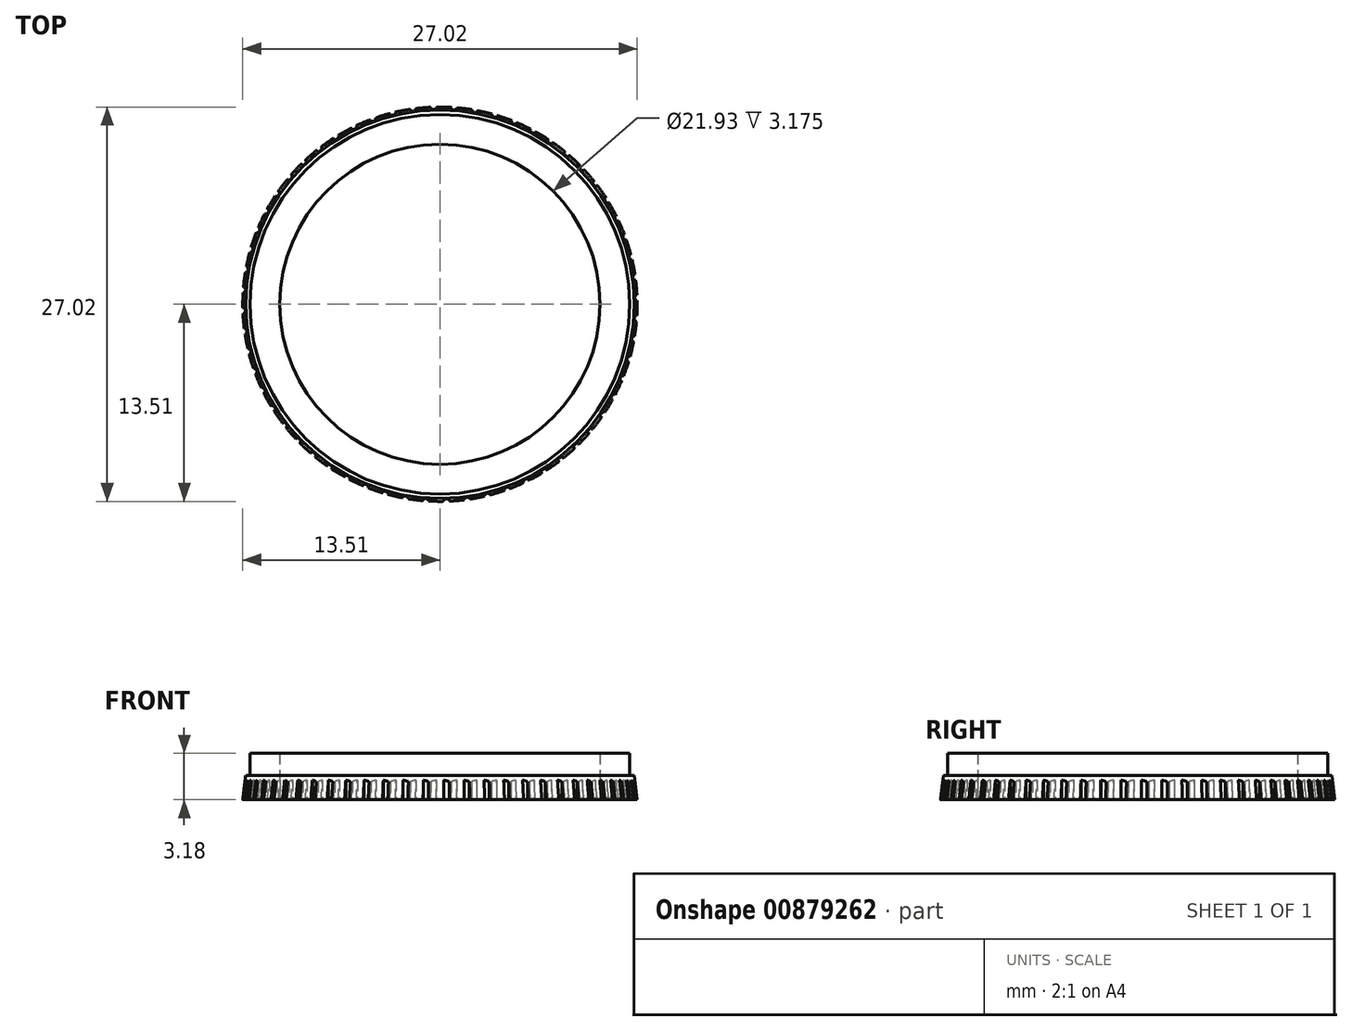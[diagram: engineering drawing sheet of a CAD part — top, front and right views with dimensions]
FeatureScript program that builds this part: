
annotation { "Feature Type Name" : "Feature", "Feature Type Description" : "" }
export const myFeature = defineFeature(function(context is Context, id is Id, definition is map)
    precondition{}
    {
        {
            var Q0;
            Q0=qCreatedBy(makeId("Front.planeOp"),FACE);
            var sketch = newSketch(context, id + "F0", { "sketchPlane" : qUnion([Q0])});
            skLineSegment(sketch, "E0", {"start": v(0, -0.58) * mm, "end": v(0, 5.66) * mm, "construction": true});
            skLineSegment(sketch, "E1", {"start": v(10.97, 0) * mm, "end": v(10.97, 3.18) * mm});
            skLineSegment(sketch, "E2", {"start": v(10.97, 3.18) * mm, "end": v(13, 3.18) * mm});
            skLineSegment(sketch, "E3", {"start": v(13, 3.18) * mm, "end": v(13, 1.66) * mm});
            skLineSegment(sketch, "E4", {"start": v(13, 1.66) * mm, "end": v(13.3, 1.66) * mm});
            skLineSegment(sketch, "E5", {"start": v(13.3, 1.66) * mm, "end": v(13.5, 0) * mm});
            skLineSegment(sketch, "E6", {"start": v(13.5, 0) * mm, "end": v(10.97, 0) * mm});
            skSolve(sketch);
        }
        {
            var Q0;
            Q0=qSketchRegion(id+"F0",true);
            var Q1;
            Q1=sQuery(id+"F0.wireOp",EDGE,"E0");
            revolve(context, id + "F1", {"surfaceOperationType" : NewSurfaceOperationType.NEW, "entities" : qUnion([Q0]), "axis" : qUnion([Q1]), "revolveType" : RevolveType.FULL});
        }
        {
            var Q0;
            Q0=makeQuery(id+"F1.opRevolve","SWEPT_FACE",FACE,{"disambiguationData":[OSD([sQuery(id+"F0.wireOp",EDGE,"E6")])]});
            var sketch = newSketch(context, id + "F2", { "sketchPlane" : qUnion([Q0])});
            skLineSegment(sketch, "E7.bottom", {"start": v(0.26, 13.55) * mm, "end": v(0.63, 13.55) * mm});
            skLineSegment(sketch, "E7.top", {"start": v(0.26, 13.34) * mm, "end": v(0.63, 13.34) * mm});
            skLineSegment(sketch, "E7.left", {"start": v(0.26, 13.55) * mm, "end": v(0.26, 13.34) * mm});
            skLineSegment(sketch, "E7.right", {"start": v(0.63, 13.55) * mm, "end": v(0.63, 13.34) * mm});
            skLineSegment(sketch, "E8.1.0", {"start": v(-1.16, 13.5) * mm, "end": v(-1.14, 13.3) * mm});
            skLineSegment(sketch, "E8.1.1", {"start": v(-0.8, 13.54) * mm, "end": v(-0.77, 13.33) * mm});
            skLineSegment(sketch, "E8.1.2", {"start": v(-1.14, 13.3) * mm, "end": v(-0.77, 13.33) * mm});
            skLineSegment(sketch, "E8.1.3", {"start": v(-1.16, 13.5) * mm, "end": v(-0.8, 13.54) * mm});
            skLineSegment(sketch, "E8.2.0", {"start": v(-2.57, 13.3) * mm, "end": v(-2.52, 13.1) * mm});
            skLineSegment(sketch, "E8.2.1", {"start": v(-2.2, 13.38) * mm, "end": v(-2.16, 13.18) * mm});
            skLineSegment(sketch, "E8.2.2", {"start": v(-2.52, 13.1) * mm, "end": v(-2.16, 13.18) * mm});
            skLineSegment(sketch, "E8.2.3", {"start": v(-2.57, 13.3) * mm, "end": v(-2.2, 13.38) * mm});
            skLineSegment(sketch, "E8.3.0", {"start": v(-3.94, 12.96) * mm, "end": v(-3.88, 12.77) * mm});
            skLineSegment(sketch, "E8.3.1", {"start": v(-3.6, 13.08) * mm, "end": v(-3.53, 12.88) * mm});
            skLineSegment(sketch, "E8.3.2", {"start": v(-3.88, 12.77) * mm, "end": v(-3.53, 12.88) * mm});
            skLineSegment(sketch, "E8.3.3", {"start": v(-3.94, 12.96) * mm, "end": v(-3.6, 13.08) * mm});
            skLineSegment(sketch, "E8.4.0", {"start": v(-5.28, 12.48) * mm, "end": v(-5.2, 12.3) * mm});
            skLineSegment(sketch, "E8.4.1", {"start": v(-4.94, 12.63) * mm, "end": v(-4.85, 12.44) * mm});
            skLineSegment(sketch, "E8.4.2", {"start": v(-5.2, 12.3) * mm, "end": v(-4.85, 12.44) * mm});
            skLineSegment(sketch, "E8.4.3", {"start": v(-5.28, 12.48) * mm, "end": v(-4.94, 12.63) * mm});
            skLineSegment(sketch, "E8.5.0", {"start": v(-6.55, 11.86) * mm, "end": v(-6.45, 11.68) * mm});
            skLineSegment(sketch, "E8.5.1", {"start": v(-6.23, 12.04) * mm, "end": v(-6.13, 11.87) * mm});
            skLineSegment(sketch, "E8.5.2", {"start": v(-6.45, 11.68) * mm, "end": v(-6.13, 11.87) * mm});
            skLineSegment(sketch, "E8.5.3", {"start": v(-6.55, 11.86) * mm, "end": v(-6.23, 12.04) * mm});
            skLineSegment(sketch, "E8.6.0", {"start": v(-7.76, 11.1) * mm, "end": v(-7.64, 10.94) * mm});
            skLineSegment(sketch, "E8.6.1", {"start": v(-7.46, 11.33) * mm, "end": v(-7.34, 11.16) * mm});
            skLineSegment(sketch, "E8.6.2", {"start": v(-7.64, 10.94) * mm, "end": v(-7.34, 11.16) * mm});
            skLineSegment(sketch, "E8.6.3", {"start": v(-7.76, 11.1) * mm, "end": v(-7.46, 11.33) * mm});
            skLineSegment(sketch, "E8.7.0", {"start": v(-8.87, 10.24) * mm, "end": v(-8.74, 10.09) * mm});
            skLineSegment(sketch, "E8.7.1", {"start": v(-8.6, 10.49) * mm, "end": v(-8.46, 10.33) * mm});
            skLineSegment(sketch, "E8.7.2", {"start": v(-8.74, 10.09) * mm, "end": v(-8.46, 10.33) * mm});
            skLineSegment(sketch, "E8.7.3", {"start": v(-8.87, 10.24) * mm, "end": v(-8.6, 10.49) * mm});
            skLineSegment(sketch, "E8.8.0", {"start": v(-9.9, 9.25) * mm, "end": v(-9.74, 9.12) * mm});
            skLineSegment(sketch, "E8.8.1", {"start": v(-9.65, 9.53) * mm, "end": v(-9.5, 9.4) * mm});
            skLineSegment(sketch, "E8.8.2", {"start": v(-9.74, 9.12) * mm, "end": v(-9.5, 9.4) * mm});
            skLineSegment(sketch, "E8.8.3", {"start": v(-9.9, 9.25) * mm, "end": v(-9.65, 9.53) * mm});
            skLineSegment(sketch, "E8.9.0", {"start": v(-10.8, 8.17) * mm, "end": v(-10.64, 8.05) * mm});
            skLineSegment(sketch, "E8.9.1", {"start": v(-10.6, 8.47) * mm, "end": v(-10.43, 8.35) * mm});
            skLineSegment(sketch, "E8.9.2", {"start": v(-10.64, 8.05) * mm, "end": v(-10.43, 8.35) * mm});
            skLineSegment(sketch, "E8.9.3", {"start": v(-10.8, 8.17) * mm, "end": v(-10.6, 8.47) * mm});
            skLineSegment(sketch, "E8.10.0", {"start": v(-11.6, 7) * mm, "end": v(-11.43, 6.9) * mm});
            skLineSegment(sketch, "E8.10.1", {"start": v(-11.42, 7.32) * mm, "end": v(-11.24, 7.21) * mm});
            skLineSegment(sketch, "E8.10.2", {"start": v(-11.43, 6.9) * mm, "end": v(-11.24, 7.21) * mm});
            skLineSegment(sketch, "E8.10.3", {"start": v(-11.6, 7) * mm, "end": v(-11.42, 7.32) * mm});
            skLineSegment(sketch, "E8.11.0", {"start": v(-12.27, 5.74) * mm, "end": v(-12.08, 5.66) * mm});
            skLineSegment(sketch, "E8.11.1", {"start": v(-12.12, 6.08) * mm, "end": v(-11.93, 6) * mm});
            skLineSegment(sketch, "E8.11.2", {"start": v(-12.08, 5.66) * mm, "end": v(-11.93, 6) * mm});
            skLineSegment(sketch, "E8.11.3", {"start": v(-12.27, 5.74) * mm, "end": v(-12.12, 6.08) * mm});
            skLineSegment(sketch, "E8.12.0", {"start": v(-12.8, 4.43) * mm, "end": v(-12.6, 4.37) * mm});
            skLineSegment(sketch, "E8.12.1", {"start": v(-12.69, 4.78) * mm, "end": v(-12.5, 4.72) * mm});
            skLineSegment(sketch, "E8.12.2", {"start": v(-12.6, 4.37) * mm, "end": v(-12.5, 4.72) * mm});
            skLineSegment(sketch, "E8.12.3", {"start": v(-12.8, 4.43) * mm, "end": v(-12.69, 4.78) * mm});
            skLineSegment(sketch, "E8.13.0", {"start": v(-13.2, 3.07) * mm, "end": v(-13, 3.02) * mm});
            skLineSegment(sketch, "E8.13.1", {"start": v(-13.12, 3.43) * mm, "end": v(-12.92, 3.39) * mm});
            skLineSegment(sketch, "E8.13.2", {"start": v(-13, 3.02) * mm, "end": v(-12.92, 3.39) * mm});
            skLineSegment(sketch, "E8.13.3", {"start": v(-13.2, 3.07) * mm, "end": v(-13.12, 3.43) * mm});
            skLineSegment(sketch, "E8.14.0", {"start": v(-13.44, 1.67) * mm, "end": v(-13.24, 1.65) * mm});
            skLineSegment(sketch, "E8.14.1", {"start": v(-13.4, 2.04) * mm, "end": v(-13.2, 2.02) * mm});
            skLineSegment(sketch, "E8.14.2", {"start": v(-13.24, 1.65) * mm, "end": v(-13.2, 2.02) * mm});
            skLineSegment(sketch, "E8.14.3", {"start": v(-13.44, 1.67) * mm, "end": v(-13.4, 2.04) * mm});
            skLineSegment(sketch, "E8.15.0", {"start": v(-13.55, 0.26) * mm, "end": v(-13.34, 0.26) * mm});
            skLineSegment(sketch, "E8.15.1", {"start": v(-13.55, 0.63) * mm, "end": v(-13.34, 0.63) * mm});
            skLineSegment(sketch, "E8.15.2", {"start": v(-13.34, 0.26) * mm, "end": v(-13.34, 0.63) * mm});
            skLineSegment(sketch, "E8.15.3", {"start": v(-13.55, 0.26) * mm, "end": v(-13.55, 0.63) * mm});
            skLineSegment(sketch, "E8.16.0", {"start": v(-13.5, -1.16) * mm, "end": v(-13.3, -1.14) * mm});
            skLineSegment(sketch, "E8.16.1", {"start": v(-13.54, -0.8) * mm, "end": v(-13.33, -0.77) * mm});
            skLineSegment(sketch, "E8.16.2", {"start": v(-13.3, -1.14) * mm, "end": v(-13.33, -0.77) * mm});
            skLineSegment(sketch, "E8.16.3", {"start": v(-13.5, -1.16) * mm, "end": v(-13.54, -0.8) * mm});
            skLineSegment(sketch, "E8.17.0", {"start": v(-13.3, -2.57) * mm, "end": v(-13.1, -2.52) * mm});
            skLineSegment(sketch, "E8.17.1", {"start": v(-13.38, -2.2) * mm, "end": v(-13.18, -2.16) * mm});
            skLineSegment(sketch, "E8.17.2", {"start": v(-13.1, -2.52) * mm, "end": v(-13.18, -2.16) * mm});
            skLineSegment(sketch, "E8.17.3", {"start": v(-13.3, -2.57) * mm, "end": v(-13.38, -2.2) * mm});
            skLineSegment(sketch, "E8.18.0", {"start": v(-12.96, -3.94) * mm, "end": v(-12.77, -3.88) * mm});
            skLineSegment(sketch, "E8.18.1", {"start": v(-13.08, -3.6) * mm, "end": v(-12.88, -3.53) * mm});
            skLineSegment(sketch, "E8.18.2", {"start": v(-12.77, -3.88) * mm, "end": v(-12.88, -3.53) * mm});
            skLineSegment(sketch, "E8.18.3", {"start": v(-12.96, -3.94) * mm, "end": v(-13.08, -3.6) * mm});
            skLineSegment(sketch, "E8.19.0", {"start": v(-12.48, -5.28) * mm, "end": v(-12.3, -5.2) * mm});
            skLineSegment(sketch, "E8.19.1", {"start": v(-12.63, -4.94) * mm, "end": v(-12.44, -4.85) * mm});
            skLineSegment(sketch, "E8.19.2", {"start": v(-12.3, -5.2) * mm, "end": v(-12.44, -4.85) * mm});
            skLineSegment(sketch, "E8.19.3", {"start": v(-12.48, -5.28) * mm, "end": v(-12.63, -4.94) * mm});
            skLineSegment(sketch, "E8.20.0", {"start": v(-11.86, -6.55) * mm, "end": v(-11.68, -6.45) * mm});
            skLineSegment(sketch, "E8.20.1", {"start": v(-12.04, -6.23) * mm, "end": v(-11.87, -6.13) * mm});
            skLineSegment(sketch, "E8.20.2", {"start": v(-11.68, -6.45) * mm, "end": v(-11.87, -6.13) * mm});
            skLineSegment(sketch, "E8.20.3", {"start": v(-11.86, -6.55) * mm, "end": v(-12.04, -6.23) * mm});
            skLineSegment(sketch, "E8.21.0", {"start": v(-11.1, -7.76) * mm, "end": v(-10.94, -7.64) * mm});
            skLineSegment(sketch, "E8.21.1", {"start": v(-11.33, -7.46) * mm, "end": v(-11.16, -7.34) * mm});
            skLineSegment(sketch, "E8.21.2", {"start": v(-10.94, -7.64) * mm, "end": v(-11.16, -7.34) * mm});
            skLineSegment(sketch, "E8.21.3", {"start": v(-11.1, -7.76) * mm, "end": v(-11.33, -7.46) * mm});
            skLineSegment(sketch, "E8.22.0", {"start": v(-10.24, -8.87) * mm, "end": v(-10.09, -8.74) * mm});
            skLineSegment(sketch, "E8.22.1", {"start": v(-10.49, -8.6) * mm, "end": v(-10.33, -8.46) * mm});
            skLineSegment(sketch, "E8.22.2", {"start": v(-10.09, -8.74) * mm, "end": v(-10.33, -8.46) * mm});
            skLineSegment(sketch, "E8.22.3", {"start": v(-10.24, -8.87) * mm, "end": v(-10.49, -8.6) * mm});
            skLineSegment(sketch, "E8.23.0", {"start": v(-9.25, -9.9) * mm, "end": v(-9.12, -9.74) * mm});
            skLineSegment(sketch, "E8.23.1", {"start": v(-9.53, -9.65) * mm, "end": v(-9.4, -9.5) * mm});
            skLineSegment(sketch, "E8.23.2", {"start": v(-9.12, -9.74) * mm, "end": v(-9.4, -9.5) * mm});
            skLineSegment(sketch, "E8.23.3", {"start": v(-9.25, -9.9) * mm, "end": v(-9.53, -9.65) * mm});
            skLineSegment(sketch, "E8.24.0", {"start": v(-8.17, -10.8) * mm, "end": v(-8.05, -10.64) * mm});
            skLineSegment(sketch, "E8.24.1", {"start": v(-8.47, -10.6) * mm, "end": v(-8.35, -10.43) * mm});
            skLineSegment(sketch, "E8.24.2", {"start": v(-8.05, -10.64) * mm, "end": v(-8.35, -10.43) * mm});
            skLineSegment(sketch, "E8.24.3", {"start": v(-8.17, -10.8) * mm, "end": v(-8.47, -10.6) * mm});
            skLineSegment(sketch, "E8.25.0", {"start": v(-7, -11.6) * mm, "end": v(-6.9, -11.43) * mm});
            skLineSegment(sketch, "E8.25.1", {"start": v(-7.32, -11.42) * mm, "end": v(-7.21, -11.24) * mm});
            skLineSegment(sketch, "E8.25.2", {"start": v(-6.9, -11.43) * mm, "end": v(-7.21, -11.24) * mm});
            skLineSegment(sketch, "E8.25.3", {"start": v(-7, -11.6) * mm, "end": v(-7.32, -11.42) * mm});
            skLineSegment(sketch, "E8.26.0", {"start": v(-5.74, -12.27) * mm, "end": v(-5.66, -12.08) * mm});
            skLineSegment(sketch, "E8.26.1", {"start": v(-6.08, -12.12) * mm, "end": v(-6, -11.93) * mm});
            skLineSegment(sketch, "E8.26.2", {"start": v(-5.66, -12.08) * mm, "end": v(-6, -11.93) * mm});
            skLineSegment(sketch, "E8.26.3", {"start": v(-5.74, -12.27) * mm, "end": v(-6.08, -12.12) * mm});
            skLineSegment(sketch, "E8.27.0", {"start": v(-4.43, -12.8) * mm, "end": v(-4.37, -12.6) * mm});
            skLineSegment(sketch, "E8.27.1", {"start": v(-4.78, -12.69) * mm, "end": v(-4.72, -12.5) * mm});
            skLineSegment(sketch, "E8.27.2", {"start": v(-4.37, -12.6) * mm, "end": v(-4.72, -12.5) * mm});
            skLineSegment(sketch, "E8.27.3", {"start": v(-4.43, -12.8) * mm, "end": v(-4.78, -12.69) * mm});
            skLineSegment(sketch, "E8.28.0", {"start": v(-3.07, -13.2) * mm, "end": v(-3.02, -13) * mm});
            skLineSegment(sketch, "E8.28.1", {"start": v(-3.43, -13.12) * mm, "end": v(-3.39, -12.92) * mm});
            skLineSegment(sketch, "E8.28.2", {"start": v(-3.02, -13) * mm, "end": v(-3.39, -12.92) * mm});
            skLineSegment(sketch, "E8.28.3", {"start": v(-3.07, -13.2) * mm, "end": v(-3.43, -13.12) * mm});
            skLineSegment(sketch, "E8.29.0", {"start": v(-1.67, -13.44) * mm, "end": v(-1.65, -13.24) * mm});
            skLineSegment(sketch, "E8.29.1", {"start": v(-2.04, -13.4) * mm, "end": v(-2.02, -13.2) * mm});
            skLineSegment(sketch, "E8.29.2", {"start": v(-1.65, -13.24) * mm, "end": v(-2.02, -13.2) * mm});
            skLineSegment(sketch, "E8.29.3", {"start": v(-1.67, -13.44) * mm, "end": v(-2.04, -13.4) * mm});
            skPoint(sketch, "E8.center", {"position": v(0, 0) * mm});
            skLineSegment(sketch, "E9.2.30.0", {"start": v(-0.26, -13.55) * mm, "end": v(-0.26, -13.34) * mm});
            skLineSegment(sketch, "E9.3.30.0", {"start": v(-0.63, -13.55) * mm, "end": v(-0.63, -13.34) * mm});
            skLineSegment(sketch, "E9.6.30.0", {"start": v(-0.26, -13.34) * mm, "end": v(-0.63, -13.34) * mm});
            skLineSegment(sketch, "E9.9.30.0", {"start": v(-0.26, -13.55) * mm, "end": v(-0.63, -13.55) * mm});
            skLineSegment(sketch, "E9.2.31.0", {"start": v(1.16, -13.5) * mm, "end": v(1.14, -13.3) * mm});
            skLineSegment(sketch, "E9.3.31.0", {"start": v(0.8, -13.54) * mm, "end": v(0.77, -13.33) * mm});
            skLineSegment(sketch, "E9.6.31.0", {"start": v(1.14, -13.3) * mm, "end": v(0.77, -13.33) * mm});
            skLineSegment(sketch, "E9.9.31.0", {"start": v(1.16, -13.5) * mm, "end": v(0.8, -13.54) * mm});
            skLineSegment(sketch, "E9.2.32.0", {"start": v(2.57, -13.3) * mm, "end": v(2.52, -13.1) * mm});
            skLineSegment(sketch, "E9.3.32.0", {"start": v(2.2, -13.38) * mm, "end": v(2.16, -13.18) * mm});
            skLineSegment(sketch, "E9.6.32.0", {"start": v(2.52, -13.1) * mm, "end": v(2.16, -13.18) * mm});
            skLineSegment(sketch, "E9.9.32.0", {"start": v(2.57, -13.3) * mm, "end": v(2.2, -13.38) * mm});
            skLineSegment(sketch, "E9.2.33.0", {"start": v(3.94, -12.96) * mm, "end": v(3.88, -12.77) * mm});
            skLineSegment(sketch, "E9.3.33.0", {"start": v(3.6, -13.08) * mm, "end": v(3.53, -12.88) * mm});
            skLineSegment(sketch, "E9.6.33.0", {"start": v(3.88, -12.77) * mm, "end": v(3.53, -12.88) * mm});
            skLineSegment(sketch, "E9.9.33.0", {"start": v(3.94, -12.96) * mm, "end": v(3.6, -13.08) * mm});
            skLineSegment(sketch, "E9.2.34.0", {"start": v(5.28, -12.48) * mm, "end": v(5.2, -12.3) * mm});
            skLineSegment(sketch, "E9.3.34.0", {"start": v(4.94, -12.63) * mm, "end": v(4.85, -12.44) * mm});
            skLineSegment(sketch, "E9.6.34.0", {"start": v(5.2, -12.3) * mm, "end": v(4.85, -12.44) * mm});
            skLineSegment(sketch, "E9.9.34.0", {"start": v(5.28, -12.48) * mm, "end": v(4.94, -12.63) * mm});
            skLineSegment(sketch, "E9.2.35.0", {"start": v(6.55, -11.86) * mm, "end": v(6.45, -11.68) * mm});
            skLineSegment(sketch, "E9.3.35.0", {"start": v(6.23, -12.04) * mm, "end": v(6.13, -11.87) * mm});
            skLineSegment(sketch, "E9.6.35.0", {"start": v(6.45, -11.68) * mm, "end": v(6.13, -11.87) * mm});
            skLineSegment(sketch, "E9.9.35.0", {"start": v(6.55, -11.86) * mm, "end": v(6.23, -12.04) * mm});
            skLineSegment(sketch, "E9.2.36.0", {"start": v(7.76, -11.1) * mm, "end": v(7.64, -10.94) * mm});
            skLineSegment(sketch, "E9.3.36.0", {"start": v(7.46, -11.33) * mm, "end": v(7.34, -11.16) * mm});
            skLineSegment(sketch, "E9.6.36.0", {"start": v(7.64, -10.94) * mm, "end": v(7.34, -11.16) * mm});
            skLineSegment(sketch, "E9.9.36.0", {"start": v(7.76, -11.1) * mm, "end": v(7.46, -11.33) * mm});
            skLineSegment(sketch, "E9.2.37.0", {"start": v(8.87, -10.24) * mm, "end": v(8.74, -10.09) * mm});
            skLineSegment(sketch, "E9.3.37.0", {"start": v(8.6, -10.49) * mm, "end": v(8.46, -10.33) * mm});
            skLineSegment(sketch, "E9.6.37.0", {"start": v(8.74, -10.09) * mm, "end": v(8.46, -10.33) * mm});
            skLineSegment(sketch, "E9.9.37.0", {"start": v(8.87, -10.24) * mm, "end": v(8.6, -10.49) * mm});
            skLineSegment(sketch, "E9.2.38.0", {"start": v(9.9, -9.25) * mm, "end": v(9.74, -9.12) * mm});
            skLineSegment(sketch, "E9.3.38.0", {"start": v(9.65, -9.53) * mm, "end": v(9.5, -9.4) * mm});
            skLineSegment(sketch, "E9.6.38.0", {"start": v(9.74, -9.12) * mm, "end": v(9.5, -9.4) * mm});
            skLineSegment(sketch, "E9.9.38.0", {"start": v(9.9, -9.25) * mm, "end": v(9.65, -9.53) * mm});
            skLineSegment(sketch, "E9.2.39.0", {"start": v(10.8, -8.17) * mm, "end": v(10.64, -8.05) * mm});
            skLineSegment(sketch, "E9.3.39.0", {"start": v(10.6, -8.47) * mm, "end": v(10.43, -8.35) * mm});
            skLineSegment(sketch, "E9.6.39.0", {"start": v(10.64, -8.05) * mm, "end": v(10.43, -8.35) * mm});
            skLineSegment(sketch, "E9.9.39.0", {"start": v(10.8, -8.17) * mm, "end": v(10.6, -8.47) * mm});
            skLineSegment(sketch, "E9.2.40.0", {"start": v(11.6, -7) * mm, "end": v(11.43, -6.9) * mm});
            skLineSegment(sketch, "E9.3.40.0", {"start": v(11.42, -7.32) * mm, "end": v(11.24, -7.21) * mm});
            skLineSegment(sketch, "E9.6.40.0", {"start": v(11.43, -6.9) * mm, "end": v(11.24, -7.21) * mm});
            skLineSegment(sketch, "E9.9.40.0", {"start": v(11.6, -7) * mm, "end": v(11.42, -7.32) * mm});
            skLineSegment(sketch, "E9.2.41.0", {"start": v(12.27, -5.74) * mm, "end": v(12.08, -5.66) * mm});
            skLineSegment(sketch, "E9.3.41.0", {"start": v(12.12, -6.08) * mm, "end": v(11.93, -6) * mm});
            skLineSegment(sketch, "E9.6.41.0", {"start": v(12.08, -5.66) * mm, "end": v(11.93, -6) * mm});
            skLineSegment(sketch, "E9.9.41.0", {"start": v(12.27, -5.74) * mm, "end": v(12.12, -6.08) * mm});
            skLineSegment(sketch, "E9.2.42.0", {"start": v(12.8, -4.43) * mm, "end": v(12.6, -4.37) * mm});
            skLineSegment(sketch, "E9.3.42.0", {"start": v(12.69, -4.78) * mm, "end": v(12.5, -4.72) * mm});
            skLineSegment(sketch, "E9.6.42.0", {"start": v(12.6, -4.37) * mm, "end": v(12.5, -4.72) * mm});
            skLineSegment(sketch, "E9.9.42.0", {"start": v(12.8, -4.43) * mm, "end": v(12.69, -4.78) * mm});
            skLineSegment(sketch, "E9.2.43.0", {"start": v(13.2, -3.07) * mm, "end": v(13, -3.02) * mm});
            skLineSegment(sketch, "E9.3.43.0", {"start": v(13.12, -3.43) * mm, "end": v(12.92, -3.39) * mm});
            skLineSegment(sketch, "E9.6.43.0", {"start": v(13, -3.02) * mm, "end": v(12.92, -3.39) * mm});
            skLineSegment(sketch, "E9.9.43.0", {"start": v(13.2, -3.07) * mm, "end": v(13.12, -3.43) * mm});
            skLineSegment(sketch, "E9.2.44.0", {"start": v(13.44, -1.67) * mm, "end": v(13.24, -1.65) * mm});
            skLineSegment(sketch, "E9.3.44.0", {"start": v(13.4, -2.04) * mm, "end": v(13.2, -2.02) * mm});
            skLineSegment(sketch, "E9.6.44.0", {"start": v(13.24, -1.65) * mm, "end": v(13.2, -2.02) * mm});
            skLineSegment(sketch, "E9.9.44.0", {"start": v(13.44, -1.67) * mm, "end": v(13.4, -2.04) * mm});
            skLineSegment(sketch, "E9.2.45.0", {"start": v(13.55, -0.26) * mm, "end": v(13.34, -0.26) * mm});
            skLineSegment(sketch, "E9.3.45.0", {"start": v(13.55, -0.63) * mm, "end": v(13.34, -0.63) * mm});
            skLineSegment(sketch, "E9.6.45.0", {"start": v(13.34, -0.26) * mm, "end": v(13.34, -0.63) * mm});
            skLineSegment(sketch, "E9.9.45.0", {"start": v(13.55, -0.26) * mm, "end": v(13.55, -0.63) * mm});
            skLineSegment(sketch, "E9.2.46.0", {"start": v(13.5, 1.16) * mm, "end": v(13.3, 1.14) * mm});
            skLineSegment(sketch, "E9.3.46.0", {"start": v(13.54, 0.8) * mm, "end": v(13.33, 0.77) * mm});
            skLineSegment(sketch, "E9.6.46.0", {"start": v(13.3, 1.14) * mm, "end": v(13.33, 0.77) * mm});
            skLineSegment(sketch, "E9.9.46.0", {"start": v(13.5, 1.16) * mm, "end": v(13.54, 0.8) * mm});
            skLineSegment(sketch, "E9.2.47.0", {"start": v(13.3, 2.57) * mm, "end": v(13.1, 2.52) * mm});
            skLineSegment(sketch, "E9.3.47.0", {"start": v(13.38, 2.2) * mm, "end": v(13.18, 2.16) * mm});
            skLineSegment(sketch, "E9.6.47.0", {"start": v(13.1, 2.52) * mm, "end": v(13.18, 2.16) * mm});
            skLineSegment(sketch, "E9.9.47.0", {"start": v(13.3, 2.57) * mm, "end": v(13.38, 2.2) * mm});
            skLineSegment(sketch, "E9.2.48.0", {"start": v(12.96, 3.94) * mm, "end": v(12.77, 3.88) * mm});
            skLineSegment(sketch, "E9.3.48.0", {"start": v(13.08, 3.6) * mm, "end": v(12.88, 3.53) * mm});
            skLineSegment(sketch, "E9.6.48.0", {"start": v(12.77, 3.88) * mm, "end": v(12.88, 3.53) * mm});
            skLineSegment(sketch, "E9.9.48.0", {"start": v(12.96, 3.94) * mm, "end": v(13.08, 3.6) * mm});
            skLineSegment(sketch, "E9.2.49.0", {"start": v(12.48, 5.28) * mm, "end": v(12.3, 5.2) * mm});
            skLineSegment(sketch, "E9.3.49.0", {"start": v(12.63, 4.94) * mm, "end": v(12.44, 4.85) * mm});
            skLineSegment(sketch, "E9.6.49.0", {"start": v(12.3, 5.2) * mm, "end": v(12.44, 4.85) * mm});
            skLineSegment(sketch, "E9.9.49.0", {"start": v(12.48, 5.28) * mm, "end": v(12.63, 4.94) * mm});
            skLineSegment(sketch, "E9.2.50.0", {"start": v(11.86, 6.55) * mm, "end": v(11.68, 6.45) * mm});
            skLineSegment(sketch, "E9.3.50.0", {"start": v(12.04, 6.23) * mm, "end": v(11.87, 6.13) * mm});
            skLineSegment(sketch, "E9.6.50.0", {"start": v(11.68, 6.45) * mm, "end": v(11.87, 6.13) * mm});
            skLineSegment(sketch, "E9.9.50.0", {"start": v(11.86, 6.55) * mm, "end": v(12.04, 6.23) * mm});
            skLineSegment(sketch, "E9.2.51.0", {"start": v(11.1, 7.76) * mm, "end": v(10.94, 7.64) * mm});
            skLineSegment(sketch, "E9.3.51.0", {"start": v(11.33, 7.46) * mm, "end": v(11.16, 7.34) * mm});
            skLineSegment(sketch, "E9.6.51.0", {"start": v(10.94, 7.64) * mm, "end": v(11.16, 7.34) * mm});
            skLineSegment(sketch, "E9.9.51.0", {"start": v(11.1, 7.76) * mm, "end": v(11.33, 7.46) * mm});
            skLineSegment(sketch, "E9.2.52.0", {"start": v(10.24, 8.87) * mm, "end": v(10.09, 8.74) * mm});
            skLineSegment(sketch, "E9.3.52.0", {"start": v(10.49, 8.6) * mm, "end": v(10.33, 8.46) * mm});
            skLineSegment(sketch, "E9.6.52.0", {"start": v(10.09, 8.74) * mm, "end": v(10.33, 8.46) * mm});
            skLineSegment(sketch, "E9.9.52.0", {"start": v(10.24, 8.87) * mm, "end": v(10.49, 8.6) * mm});
            skLineSegment(sketch, "E9.2.53.0", {"start": v(9.25, 9.9) * mm, "end": v(9.12, 9.74) * mm});
            skLineSegment(sketch, "E9.3.53.0", {"start": v(9.53, 9.65) * mm, "end": v(9.4, 9.5) * mm});
            skLineSegment(sketch, "E9.6.53.0", {"start": v(9.12, 9.74) * mm, "end": v(9.4, 9.5) * mm});
            skLineSegment(sketch, "E9.9.53.0", {"start": v(9.25, 9.9) * mm, "end": v(9.53, 9.65) * mm});
            skLineSegment(sketch, "E9.2.54.0", {"start": v(8.17, 10.8) * mm, "end": v(8.05, 10.64) * mm});
            skLineSegment(sketch, "E9.3.54.0", {"start": v(8.47, 10.6) * mm, "end": v(8.35, 10.43) * mm});
            skLineSegment(sketch, "E9.6.54.0", {"start": v(8.05, 10.64) * mm, "end": v(8.35, 10.43) * mm});
            skLineSegment(sketch, "E9.9.54.0", {"start": v(8.17, 10.8) * mm, "end": v(8.47, 10.6) * mm});
            skLineSegment(sketch, "E9.2.55.0", {"start": v(7, 11.6) * mm, "end": v(6.9, 11.43) * mm});
            skLineSegment(sketch, "E9.3.55.0", {"start": v(7.32, 11.42) * mm, "end": v(7.21, 11.24) * mm});
            skLineSegment(sketch, "E9.6.55.0", {"start": v(6.9, 11.43) * mm, "end": v(7.21, 11.24) * mm});
            skLineSegment(sketch, "E9.9.55.0", {"start": v(7, 11.6) * mm, "end": v(7.32, 11.42) * mm});
            skLineSegment(sketch, "E9.2.56.0", {"start": v(5.74, 12.27) * mm, "end": v(5.66, 12.08) * mm});
            skLineSegment(sketch, "E9.3.56.0", {"start": v(6.08, 12.12) * mm, "end": v(6, 11.93) * mm});
            skLineSegment(sketch, "E9.6.56.0", {"start": v(5.66, 12.08) * mm, "end": v(6, 11.93) * mm});
            skLineSegment(sketch, "E9.9.56.0", {"start": v(5.74, 12.27) * mm, "end": v(6.08, 12.12) * mm});
            skLineSegment(sketch, "E9.2.57.0", {"start": v(4.43, 12.8) * mm, "end": v(4.37, 12.6) * mm});
            skLineSegment(sketch, "E9.3.57.0", {"start": v(4.78, 12.69) * mm, "end": v(4.72, 12.5) * mm});
            skLineSegment(sketch, "E9.6.57.0", {"start": v(4.37, 12.6) * mm, "end": v(4.72, 12.5) * mm});
            skLineSegment(sketch, "E9.9.57.0", {"start": v(4.43, 12.8) * mm, "end": v(4.78, 12.69) * mm});
            skLineSegment(sketch, "E9.2.58.0", {"start": v(3.07, 13.2) * mm, "end": v(3.02, 13) * mm});
            skLineSegment(sketch, "E9.3.58.0", {"start": v(3.43, 13.12) * mm, "end": v(3.39, 12.92) * mm});
            skLineSegment(sketch, "E9.6.58.0", {"start": v(3.02, 13) * mm, "end": v(3.39, 12.92) * mm});
            skLineSegment(sketch, "E9.9.58.0", {"start": v(3.07, 13.2) * mm, "end": v(3.43, 13.12) * mm});
            skLineSegment(sketch, "E9.2.59.0", {"start": v(1.67, 13.44) * mm, "end": v(1.65, 13.24) * mm});
            skLineSegment(sketch, "E9.3.59.0", {"start": v(2.04, 13.4) * mm, "end": v(2.02, 13.2) * mm});
            skLineSegment(sketch, "E9.6.59.0", {"start": v(1.65, 13.24) * mm, "end": v(2.02, 13.2) * mm});
            skLineSegment(sketch, "E9.9.59.0", {"start": v(1.67, 13.44) * mm, "end": v(2.04, 13.4) * mm});
            skSolve(sketch);
        }
        {
            var Q0;
            Q0=qSketchRegion(id+"F2",true);
            extrude(context, id + "F3", {"entities" : qUnion([Q0]), "operationType" : NewBodyOperationType.REMOVE, "oppositeDirection" : true, "depth" : 25.4 * mm, "offsetDistance" : 25.4 * mm});
        }
    });
